# Revit family: 27927CHN_new
name_source: partatom
category: Furniture
revit_build: Autodesk Revit 2018 (Build: 20170223_1515(x64)
units: mm (PartAtom-declared; Revit-internal decimal feet)

## family parameters
Always vertical = No
Cut with Voids When Loaded = No
OmniClass Number = 23.40.20.00
OmniClass Title = General Furniture and Specialties
Room Calculation Point = No
Shared = No
Work Plane-Based = Yes

## types (1)
- 707 Matt White
    Always visible = Yes
    BIMobject category = Sanitary Accessories
    Default Elevation = 1219.2 mm  [stored 4 ft]
    Design country = Germany
    EAN code = 4059625353066
    Edition number = 1
    IFC Classification = Sanitary Terminal
    Installation instructions = https://www.hansgrohe.com
    Manufacturer country = Germany
    Manufacturer name = hansgrohe
    Material 1 = Hansgrohe - WallStoris - 707 Matt White
    Material main = Plastic
    Product Guid = 7fa2d8cd-4725-42db-bfb3-dc5faff6239c
    Product SKU = 27927CHN
    Product data url = https://www.bimobject.com
    Product family = WallStoris
    Product group = Toilet brush holders
    Product name = 27927CHN WallStoris Toilet brush holder
    Product url = https://www.hansgrohe.com
    QR code = https://www.bimobject.com
    Technical description = https://www.hansgrohe.com

note: [stored X ft] marks values corroborated as IEEE doubles in the binary element streams (Revit-internal decimal feet)

## geometry (parser evidence)
native form markers: Sweep x2
no freeform markers — native parametric forms only
